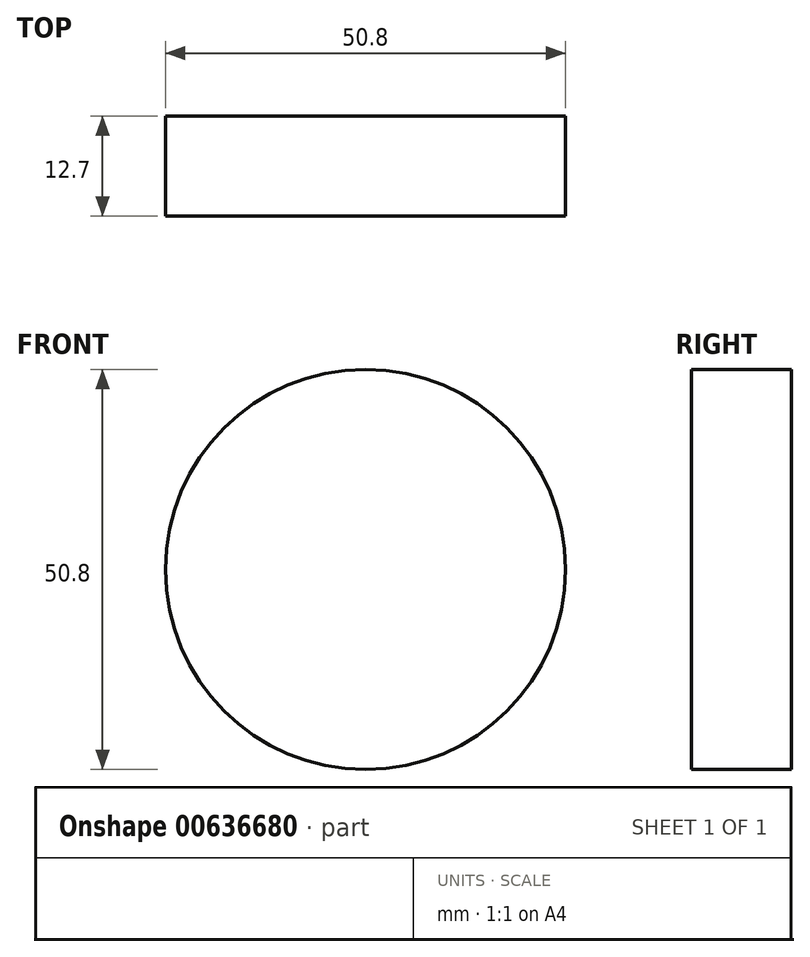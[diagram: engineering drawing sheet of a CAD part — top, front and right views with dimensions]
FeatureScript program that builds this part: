
annotation { "Feature Type Name" : "Feature", "Feature Type Description" : "" }
export const myFeature = defineFeature(function(context is Context, id is Id, definition is map)
    precondition{}
    {
        {
            var Q0;
            Q0=qCreatedBy(makeId("Front.planeOp"),FACE);
            var sketch = newSketch(context, id + "F0", { "sketchPlane" : qUnion([Q0])});
            skCircle(sketch, "E0", {"center": v(0, 0) * mm, "radius": 25.4 * mm});
            skSolve(sketch);
        }
        {
            var Q0;
            Q0=makeQuery(id+"F0.imprint","IMPRINT",FACE,{"disambiguationData":[TD([[makeQuery(id+"F0.imprint","IMPRINT",EDGE,{"derivedFrom":sQuery(id+"F0.wireOp",EDGE,"E0")}),1.0]])]});
            extrude(context, id + "F1", {"entities" : qUnion([Q0]), "depth" : 12.7 * mm, "offsetDistance" : 25.4 * mm});
        }
        {
            var Q0;
            Q0=makeQuery(id+"F1.opExtrude","CAP_FACE",FACE,{"disambiguationData":[OSD([sQuery(id+"F0.wireOp",EDGE,"E0")])],"isStart":false});
            var sketch = newSketch(context, id + "F2", { "sketchPlane" : qUnion([Q0])});
            skLineSegment(sketch, "E1", {"start": v(0, 25.4) * mm, "end": v(0, 19.05) * mm, "construction": true});
            skCircle(sketch, "E2", {"center": v(0, 19.05) * mm, "radius": 3.18 * mm});
            skCircle(sketch, "E3.1.0", {"center": v(-16.5, -9.52) * mm, "radius": 3.18 * mm});
            skCircle(sketch, "E3.2.0", {"center": v(16.5, -9.53) * mm, "radius": 3.18 * mm});
            skPoint(sketch, "E3.center", {"position": v(0, 0) * mm});
            skSolve(sketch);
        }
    });
